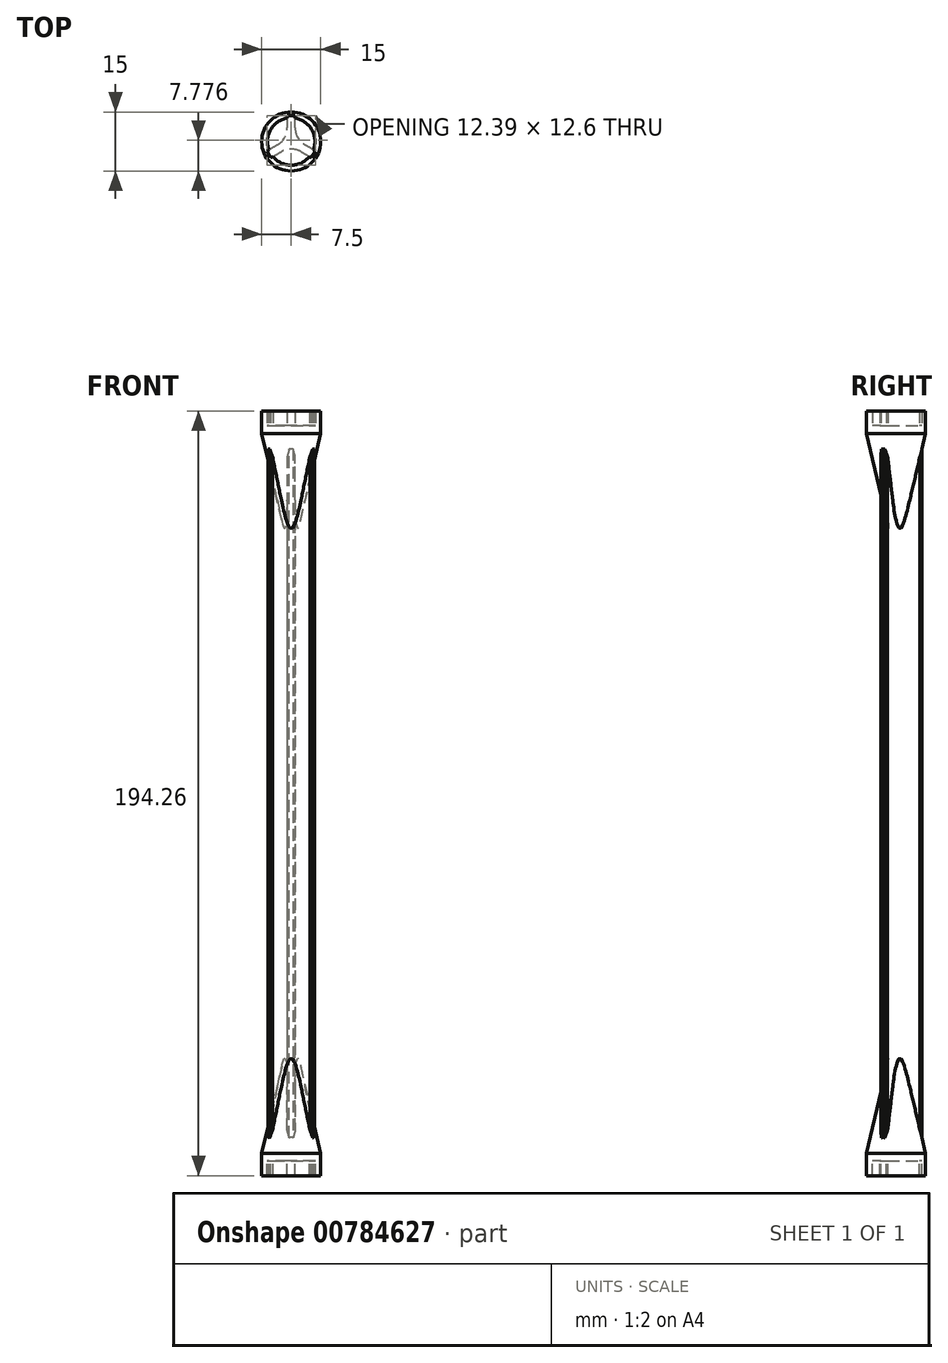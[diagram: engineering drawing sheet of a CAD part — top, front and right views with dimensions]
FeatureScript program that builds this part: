
annotation { "Feature Type Name" : "Feature", "Feature Type Description" : "" }
export const myFeature = defineFeature(function(context is Context, id is Id, definition is map)
    precondition{}
    {
        {
            var Q0;
            Q0=qCreatedBy(makeId("Top.planeOp"),FACE);
            var sketch = newSketch(context, id + "F0", { "sketchPlane" : qUnion([Q0])});
            skLineSegment(sketch, "E0", {"start": v(-1, 6.58) * mm, "end": v(1, 6.58) * mm});
            skLineSegment(sketch, "E1", {"start": v(1, 6.58) * mm, "end": v(1, 0.58) * mm});
            skLineSegment(sketch, "E2", {"start": v(1, 0.58) * mm, "end": v(6.2, -2.42) * mm});
            skLineSegment(sketch, "E3", {"start": v(6.2, -2.42) * mm, "end": v(5.2, -4.15) * mm});
            skLineSegment(sketch, "E4", {"start": v(5.2, -4.15) * mm, "end": v(0, -1.15) * mm});
            skLineSegment(sketch, "E5", {"start": v(0, -1.15) * mm, "end": v(-5.2, -4.15) * mm});
            skLineSegment(sketch, "E6", {"start": v(-5.2, -4.15) * mm, "end": v(-6.2, -2.42) * mm});
            skLineSegment(sketch, "E7", {"start": v(-6.2, -2.42) * mm, "end": v(-1, 0.58) * mm});
            skLineSegment(sketch, "E8", {"start": v(-1, 0.58) * mm, "end": v(-1, 6.58) * mm});
            skLineSegment(sketch, "E9", {"start": v(0, -1.15) * mm, "end": v(0, 0) * mm, "construction": true});
            skLineSegment(sketch, "E10", {"start": v(0, 0) * mm, "end": v(-1, 0.58) * mm, "construction": true});
            skLineSegment(sketch, "E11", {"start": v(0, 0) * mm, "end": v(1, 0.58) * mm, "construction": true});
            skSolve(sketch);
        }
        {
            var Q0;
            Q0=makeQuery(id+"F0.imprint","IMPRINT",FACE,{"disambiguationData":[TD([[makeQuery(id+"F0.imprint","IMPRINT",EDGE,{"derivedFrom":sQuery(id+"F0.wireOp",EDGE,"E0")}),-1.0]])]});
            extrude(context, id + "F1", {"entities" : qUnion([Q0]), "depth" : (100 - (1.66 + 15.48) / 2) * mm, "offsetDistance" : 25 * mm});
        }
        {
            var Q0;
            Q0=makeQuery(id+"F1.opExtrude","CAP_FACE",FACE,{"disambiguationData":[OSD([sQuery(id+"F0.wireOp",EDGE,"E0"),sQuery(id+"F0.wireOp",EDGE,"E1"),sQuery(id+"F0.wireOp",EDGE,"E2"),sQuery(id+"F0.wireOp",EDGE,"E3"),sQuery(id+"F0.wireOp",EDGE,"E4"),sQuery(id+"F0.wireOp",EDGE,"E5"),sQuery(id+"F0.wireOp",EDGE,"E6"),sQuery(id+"F0.wireOp",EDGE,"E7"),sQuery(id+"F0.wireOp",EDGE,"E8")])],"isStart":false});
            var sketch = newSketch(context, id + "F2", { "sketchPlane" : qUnion([Q0])});
            skCircle(sketch, "E12", {"center": v(0, 0) * mm, "radius": 6.03 * mm});
            skCircle(sketch, "E13", {"center": v(0, 0) * mm, "radius": 7.5 * mm});
            skSolve(sketch);
        }
        {
            var Q0;
            Q0=makeQuery(id+"F2.imprint","IMPRINT",FACE,{"disambiguationData":[TD([[makeQuery(id+"F2.imprint","IMPRINT",EDGE,{"derivedFrom":sQuery(id+"F2.wireOp",EDGE,"E13")}),1.0]])]});
            var Q1;
            {var subQ3=sQuery(id+"F2.wireOp",EDGE,"E12");var subQ5=makeQuery(id+"F1.opExtrude","CAP_EDGE",EDGE,{"disambiguationData":[OSD([sQuery(id+"F0.wireOp",EDGE,"E8")])],"isStart":false});var subQ6=makeQuery(id+"F2.imprint","INTERSECT",VERTEX,{"derivedFrom":[subQ5,subQ3]});Q1=makeQuery(id+"F2.imprint","IMPRINT",FACE,{"disambiguationData":[TD([[makeQuery(id+"F2.imprint","IMPRINT",EDGE,{"disambiguationData":[TD([[subQ6,1.0]])],"derivedFrom":subQ3}),1.0]])]});}
            var Q2;
            {var subQ0=sQuery(id+"F2.wireOp",EDGE,"E12");var subQ1=makeQuery(id+"F1.opExtrude","CAP_EDGE",EDGE,{"disambiguationData":[OSD([sQuery(id+"F0.wireOp",EDGE,"E1")])],"isStart":false});var subQ2=makeQuery(id+"F2.imprint","INTERSECT",VERTEX,{"derivedFrom":[subQ1,subQ0]});Q2=makeQuery(id+"F2.imprint","IMPRINT",FACE,{"disambiguationData":[TD([[makeQuery(id+"F2.imprint","IMPRINT",EDGE,{"disambiguationData":[TD([[subQ2,1.0]])],"derivedFrom":subQ0}),1.0]])]});}
            var Q3;
            {var subQ0=sQuery(id+"F2.wireOp",EDGE,"E12");var subQ1=makeQuery(id+"F1.opExtrude","CAP_EDGE",EDGE,{"disambiguationData":[OSD([sQuery(id+"F0.wireOp",EDGE,"E5")])],"isStart":false});var subQ2=makeQuery(id+"F2.imprint","INTERSECT",VERTEX,{"derivedFrom":[subQ1,subQ0]});Q3=makeQuery(id+"F2.imprint","IMPRINT",FACE,{"disambiguationData":[TD([[makeQuery(id+"F2.imprint","IMPRINT",EDGE,{"disambiguationData":[TD([[subQ2,-1.0]])],"derivedFrom":subQ0}),1.0]])]});}
            var Q4;
            {var subQ0=sQuery(id+"F2.wireOp",EDGE,"E12");var subQ1=makeQuery(id+"F1.opExtrude","CAP_EDGE",EDGE,{"disambiguationData":[OSD([sQuery(id+"F0.wireOp",EDGE,"E8")])],"isStart":false});var subQ2=makeQuery(id+"F2.imprint","INTERSECT",VERTEX,{"derivedFrom":[subQ1,subQ0]});Q4=makeQuery(id+"F2.imprint","IMPRINT",FACE,{"disambiguationData":[TD([[makeQuery(id+"F2.imprint","IMPRINT",EDGE,{"disambiguationData":[TD([[subQ2,-1.0]])],"derivedFrom":subQ0}),1.0]])]});}
            var Q5;
            {var subQ5=makeQuery(id+"F1.opExtrude","CAP_EDGE",EDGE,{"disambiguationData":[OSD([sQuery(id+"F0.wireOp",EDGE,"E6")])],"isStart":false});Q5=makeQuery(id+"F2.imprint","IMPRINT",FACE,{"disambiguationData":[TD([[makeQuery(id+"F2.imprint","IMPRINT",EDGE,{"derivedFrom":subQ5}),-1.0]])]});}
            var Q6;
            {var subQ5=makeQuery(id+"F1.opExtrude","CAP_EDGE",EDGE,{"disambiguationData":[OSD([sQuery(id+"F0.wireOp",EDGE,"E3")])],"isStart":false});Q6=makeQuery(id+"F2.imprint","IMPRINT",FACE,{"disambiguationData":[TD([[makeQuery(id+"F2.imprint","IMPRINT",EDGE,{"derivedFrom":subQ5}),-1.0]])]});}
            var Q7;
            {var subQ5=makeQuery(id+"F1.opExtrude","CAP_EDGE",EDGE,{"disambiguationData":[OSD([sQuery(id+"F0.wireOp",EDGE,"E0")])],"isStart":false});Q7=makeQuery(id+"F2.imprint","IMPRINT",FACE,{"disambiguationData":[TD([[makeQuery(id+"F2.imprint","IMPRINT",EDGE,{"derivedFrom":subQ5}),-1.0]])]});}
            extrude(context, id + "F3", {"entities" : qUnion([Q0, Q1, Q2, Q3, Q4, Q5, Q6, Q7]), "operationType" : NewBodyOperationType.ADD, "depth" : 2 * mm, "offsetDistance" : 25 * mm});
        }
        {
            var Q0;
            Q0=makeQuery(id+"F2.imprint","IMPRINT",FACE,{"disambiguationData":[TD([[makeQuery(id+"F2.imprint","IMPRINT",EDGE,{"derivedFrom":sQuery(id+"F2.wireOp",EDGE,"E13")}),1.0]])]});
            extrude(context, id + "F4", {"entities" : qUnion([Q0]), "operationType" : NewBodyOperationType.ADD, "depth" : (3.7 + 2) * mm, "offsetDistance" : 25 * mm});
        }
        {
            var Q0;
            Q0=makeQuery(id+"F1.opExtrude","SWEPT_EDGE",EDGE,{"disambiguationData":[OSD([sQuery(id+"F0.wireOp",EDGE,"E7"),sQuery(id+"F0.wireOp",EDGE,"E8")])]});
            var Q1;
            Q1=makeQuery(id+"F1.opExtrude","SWEPT_EDGE",EDGE,{"disambiguationData":[OSD([sQuery(id+"F0.wireOp",EDGE,"E1"),sQuery(id+"F0.wireOp",EDGE,"E2")])]});
            var Q2;
            Q2=makeQuery(id+"F1.opExtrude","SWEPT_EDGE",EDGE,{"disambiguationData":[OSD([sQuery(id+"F0.wireOp",EDGE,"E4"),sQuery(id+"F0.wireOp",EDGE,"E5")])]});
            fillet(context, id + "F5", {"entities" : qUnion([Q0, Q1, Q2]), "tangentPropagation" : true, "radius" : 5 * mm, "defaultsChanged" : false, "vertexSettings" : [], "allowEdgeOverflow" : false});
        }
        {
            var Q0;
            Q0=makeQuery(id+"F2.imprint","IMPRINT",FACE,{"disambiguationData":[TD([[makeQuery(id+"F2.imprint","IMPRINT",EDGE,{"derivedFrom":sQuery(id+"F2.wireOp",EDGE,"E13")}),1.0]])]});
            var Q1;
            {var subQ5=makeQuery(id+"F1.opExtrude","CAP_EDGE",EDGE,{"disambiguationData":[OSD([sQuery(id+"F0.wireOp",EDGE,"E6")])],"isStart":false});Q1=makeQuery(id+"F2.imprint","IMPRINT",FACE,{"disambiguationData":[TD([[makeQuery(id+"F2.imprint","IMPRINT",EDGE,{"derivedFrom":subQ5}),-1.0]])]});}
            var Q2;
            {var subQ0=sQuery(id+"F2.wireOp",EDGE,"E12");var subQ1=makeQuery(id+"F1.opExtrude","CAP_EDGE",EDGE,{"disambiguationData":[OSD([sQuery(id+"F0.wireOp",EDGE,"E8")])],"isStart":false});var subQ2=makeQuery(id+"F2.imprint","INTERSECT",VERTEX,{"derivedFrom":[subQ1,subQ0]});Q2=makeQuery(id+"F2.imprint","IMPRINT",FACE,{"disambiguationData":[TD([[makeQuery(id+"F2.imprint","IMPRINT",EDGE,{"disambiguationData":[TD([[subQ2,-1.0]])],"derivedFrom":subQ0}),1.0]])]});}
            var Q3;
            {var subQ3=sQuery(id+"F2.wireOp",EDGE,"E12");var subQ5=makeQuery(id+"F1.opExtrude","CAP_EDGE",EDGE,{"disambiguationData":[OSD([sQuery(id+"F0.wireOp",EDGE,"E8")])],"isStart":false});var subQ6=makeQuery(id+"F2.imprint","INTERSECT",VERTEX,{"derivedFrom":[subQ5,subQ3]});Q3=makeQuery(id+"F2.imprint","IMPRINT",FACE,{"disambiguationData":[TD([[makeQuery(id+"F2.imprint","IMPRINT",EDGE,{"disambiguationData":[TD([[subQ6,1.0]])],"derivedFrom":subQ3}),1.0]])]});}
            var Q4;
            {var subQ0=sQuery(id+"F2.wireOp",EDGE,"E12");var subQ1=makeQuery(id+"F1.opExtrude","CAP_EDGE",EDGE,{"disambiguationData":[OSD([sQuery(id+"F0.wireOp",EDGE,"E5")])],"isStart":false});var subQ2=makeQuery(id+"F2.imprint","INTERSECT",VERTEX,{"derivedFrom":[subQ1,subQ0]});Q4=makeQuery(id+"F2.imprint","IMPRINT",FACE,{"disambiguationData":[TD([[makeQuery(id+"F2.imprint","IMPRINT",EDGE,{"disambiguationData":[TD([[subQ2,-1.0]])],"derivedFrom":subQ0}),1.0]])]});}
            var Q5;
            {var subQ0=sQuery(id+"F2.wireOp",EDGE,"E12");var subQ1=makeQuery(id+"F1.opExtrude","CAP_EDGE",EDGE,{"disambiguationData":[OSD([sQuery(id+"F0.wireOp",EDGE,"E1")])],"isStart":false});var subQ2=makeQuery(id+"F2.imprint","INTERSECT",VERTEX,{"derivedFrom":[subQ1,subQ0]});Q5=makeQuery(id+"F2.imprint","IMPRINT",FACE,{"disambiguationData":[TD([[makeQuery(id+"F2.imprint","IMPRINT",EDGE,{"disambiguationData":[TD([[subQ2,1.0]])],"derivedFrom":subQ0}),1.0]])]});}
            var Q6;
            {var subQ5=makeQuery(id+"F1.opExtrude","CAP_EDGE",EDGE,{"disambiguationData":[OSD([sQuery(id+"F0.wireOp",EDGE,"E3")])],"isStart":false});Q6=makeQuery(id+"F2.imprint","IMPRINT",FACE,{"disambiguationData":[TD([[makeQuery(id+"F2.imprint","IMPRINT",EDGE,{"derivedFrom":subQ5}),-1.0]])]});}
            var Q7;
            {var subQ5=makeQuery(id+"F1.opExtrude","CAP_EDGE",EDGE,{"disambiguationData":[OSD([sQuery(id+"F0.wireOp",EDGE,"E0")])],"isStart":false});Q7=makeQuery(id+"F2.imprint","IMPRINT",FACE,{"disambiguationData":[TD([[makeQuery(id+"F2.imprint","IMPRINT",EDGE,{"derivedFrom":subQ5}),-1.0]])]});}
            extrude(context, id + "F6", {"entities" : qUnion([Q0, Q1, Q2, Q3, Q4, Q5, Q6, Q7]), "operationType" : NewBodyOperationType.ADD, "oppositeDirection" : true, "depth" : 25 * mm, "offsetDistance" : 25 * mm, "hasDraft" : true, "draftAngle" : 13 * degree, "draftPullDirection" : true});
        }
        {
            var Q0;
            Q0=makeQuery(id+"F1.opExtrude","SWEPT_EDGE",EDGE,{"disambiguationData":[OSD([sQuery(id+"F0.wireOp",EDGE,"E6"),sQuery(id+"F0.wireOp",EDGE,"E7")])]});
            var Q1;
            Q1=makeQuery(id+"F1.opExtrude","SWEPT_EDGE",EDGE,{"disambiguationData":[OSD([sQuery(id+"F0.wireOp",EDGE,"E0"),sQuery(id+"F0.wireOp",EDGE,"E8")])]});
            var Q2;
            Q2=makeQuery(id+"F1.opExtrude","SWEPT_EDGE",EDGE,{"disambiguationData":[OSD([sQuery(id+"F0.wireOp",EDGE,"E0"),sQuery(id+"F0.wireOp",EDGE,"E1")])]});
            var Q3;
            Q3=makeQuery(id+"F1.opExtrude","SWEPT_EDGE",EDGE,{"disambiguationData":[OSD([sQuery(id+"F0.wireOp",EDGE,"E2"),sQuery(id+"F0.wireOp",EDGE,"E3")])]});
            var Q4;
            Q4=makeQuery(id+"F1.opExtrude","SWEPT_EDGE",EDGE,{"disambiguationData":[OSD([sQuery(id+"F0.wireOp",EDGE,"E3"),sQuery(id+"F0.wireOp",EDGE,"E4")])]});
            var Q5;
            Q5=makeQuery(id+"F1.opExtrude","SWEPT_EDGE",EDGE,{"disambiguationData":[OSD([sQuery(id+"F0.wireOp",EDGE,"E5"),sQuery(id+"F0.wireOp",EDGE,"E6")])]});
            chamfer(context, id + "F7", {"entities" : qUnion([Q0, Q1, Q2, Q3, Q4, Q5]), "width" : 0.5 * mm, "tangentPropagation" : true});
        }
        {
            var Q0;
            Q0=makeQuery(id+"F1.opExtrude","SWEPT_BODY",BODY,{"disambiguationData":[OSD([sQuery(id+"F0.wireOp",EDGE,"E0"),sQuery(id+"F0.wireOp",EDGE,"E1"),sQuery(id+"F0.wireOp",EDGE,"E2"),sQuery(id+"F0.wireOp",EDGE,"E3"),sQuery(id+"F0.wireOp",EDGE,"E4"),sQuery(id+"F0.wireOp",EDGE,"E5"),sQuery(id+"F0.wireOp",EDGE,"E6"),sQuery(id+"F0.wireOp",EDGE,"E7"),sQuery(id+"F0.wireOp",EDGE,"E8")])]});
            var Q1;
            Q1=qCreatedBy(makeId("Top.planeOp"),FACE);
            mirror(context, id + "F8", {"operationType" : NewBodyOperationType.ADD, "entities" : qUnion([Q0]), "mirrorPlane" : qUnion([Q1])});
        }
    });
